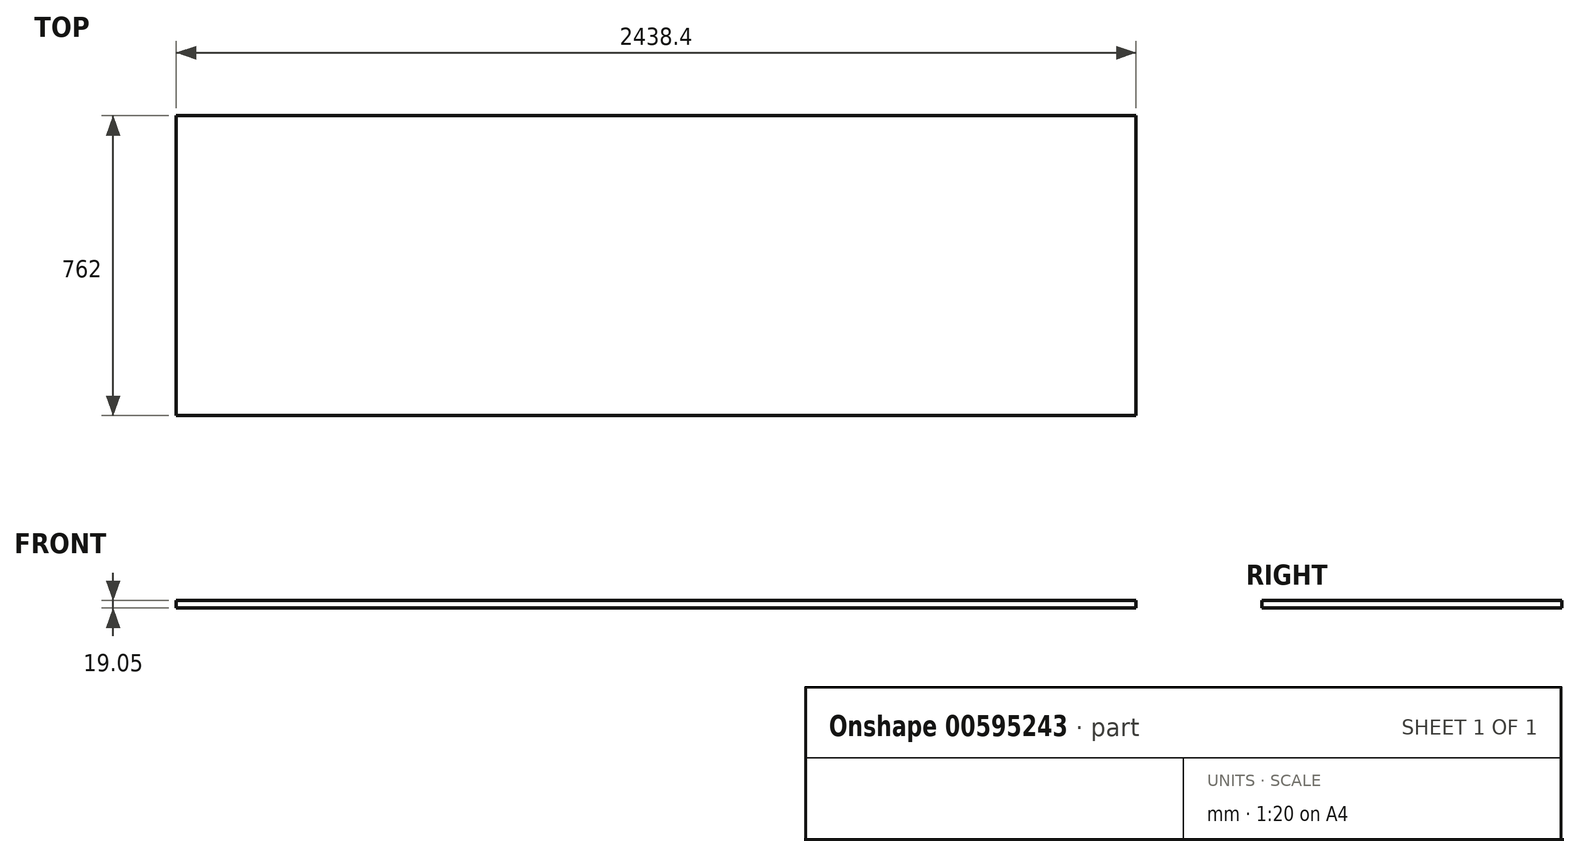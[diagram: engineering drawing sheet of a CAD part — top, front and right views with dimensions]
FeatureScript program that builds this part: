
annotation { "Feature Type Name" : "Feature", "Feature Type Description" : "" }
export const myFeature = defineFeature(function(context is Context, id is Id, definition is map)
    precondition{}
    {
        {
            var Q0;
            Q0=qCreatedBy(makeId("Top.planeOp"),FACE);
            var sketch = newSketch(context, id + "F0", { "sketchPlane" : qUnion([Q0])});
            skLineSegment(sketch, "E0.bottom", {"start": v(3810, -4419.6) * mm, "end": v(-3810, -4419.6) * mm});
            skLineSegment(sketch, "E0.top", {"start": v(3810, 4419.6) * mm, "end": v(-3810, 4419.6) * mm});
            skLineSegment(sketch, "E0.left", {"start": v(3810, -4419.6) * mm, "end": v(3810, 4419.6) * mm});
            skLineSegment(sketch, "E0.right", {"start": v(-3810, -4419.6) * mm, "end": v(-3810, 4419.6) * mm});
            skPoint(sketch, "E0.middle", {"position": v(0, 0) * mm});
            skLineSegment(sketch, "E1.top", {"start": v(3810, 1676.4) * mm, "end": v(1981.2, 1676.4) * mm});
            skLineSegment(sketch, "E1.right", {"start": v(1981.2, 4419.6) * mm, "end": v(1981.2, 1676.4) * mm});
            skLineSegment(sketch, "E2.bottom", {"start": v(-3810, -4419.6) * mm, "end": v(-3352.8, -4419.6) * mm});
            skLineSegment(sketch, "E2.top", {"start": v(-3810, -3962.4) * mm, "end": v(-3352.8, -3962.4) * mm});
            skLineSegment(sketch, "E2.left", {"start": v(-3810, -4419.6) * mm, "end": v(-3810, -3962.4) * mm});
            skLineSegment(sketch, "E2.right", {"start": v(-3352.8, -4419.6) * mm, "end": v(-3352.8, -3962.4) * mm});
            skLineSegment(sketch, "E3.bottom", {"start": v(457.2, -4419.6) * mm, "end": v(0, -4419.6) * mm});
            skLineSegment(sketch, "E3.top", {"start": v(457.2, -3962.4) * mm, "end": v(0, -3962.4) * mm});
            skLineSegment(sketch, "E3.left", {"start": v(457.2, -4419.6) * mm, "end": v(457.2, -3962.4) * mm});
            skLineSegment(sketch, "E3.right", {"start": v(0, -4419.6) * mm, "end": v(0, -3962.4) * mm});
            skLineSegment(sketch, "E4.bottom", {"start": v(3810, -4419.6) * mm, "end": v(3352.8, -4419.6) * mm});
            skLineSegment(sketch, "E4.top", {"start": v(3810, -3962.4) * mm, "end": v(3352.8, -3962.4) * mm});
            skLineSegment(sketch, "E4.left", {"start": v(3810, -4419.6) * mm, "end": v(3810, -3962.4) * mm});
            skLineSegment(sketch, "E4.right", {"start": v(3352.8, -4419.6) * mm, "end": v(3352.8, -3962.4) * mm});
            skLineSegment(sketch, "E5.bottom", {"start": v(-3259.23, 4114.8) * mm, "end": v(-820.83, 4114.8) * mm});
            skLineSegment(sketch, "E5.top", {"start": v(-3259.23, 3352.8) * mm, "end": v(-820.83, 3352.8) * mm});
            skLineSegment(sketch, "E5.left", {"start": v(-3259.23, 4114.8) * mm, "end": v(-3259.23, 3352.8) * mm});
            skLineSegment(sketch, "E5.right", {"start": v(-820.83, 4114.8) * mm, "end": v(-820.83, 3352.8) * mm});
            skLineSegment(sketch, "E6.bottom", {"start": v(-1676.4, 716.47) * mm, "end": v(-457.2, 716.47) * mm});
            skLineSegment(sketch, "E6.top", {"start": v(-1676.4, -1721.93) * mm, "end": v(-457.2, -1721.93) * mm});
            skLineSegment(sketch, "E6.left", {"start": v(-1676.4, 716.47) * mm, "end": v(-1676.4, -1721.93) * mm});
            skLineSegment(sketch, "E6.right", {"start": v(-457.2, 716.47) * mm, "end": v(-457.2, -1721.93) * mm});
            skLineSegment(sketch, "E7.bottom", {"start": v(-304.8, 4419.6) * mm, "end": v(152.4, 4419.6) * mm});
            skLineSegment(sketch, "E7.top", {"start": v(-304.8, 3962.4) * mm, "end": v(152.4, 3962.4) * mm});
            skLineSegment(sketch, "E7.left", {"start": v(-304.8, 4419.6) * mm, "end": v(-304.8, 3962.4) * mm});
            skLineSegment(sketch, "E7.right", {"start": v(152.4, 4419.6) * mm, "end": v(152.4, 3962.4) * mm});
            skLineSegment(sketch, "E8.bottom", {"start": v(1219.2, 4419.6) * mm, "end": v(1981.2, 4419.6) * mm});
            skLineSegment(sketch, "E8.top", {"start": v(1219.2, 1981.2) * mm, "end": v(1981.2, 1981.2) * mm});
            skLineSegment(sketch, "E8.left", {"start": v(1219.2, 4419.6) * mm, "end": v(1219.2, 1981.2) * mm});
            skLineSegment(sketch, "E8.right", {"start": v(1981.2, 4419.6) * mm, "end": v(1981.2, 1981.2) * mm});
            skLineSegment(sketch, "E9.bottom", {"start": v(1676.4, -70.73) * mm, "end": v(2590.8, -70.73) * mm});
            skLineSegment(sketch, "E9.top", {"start": v(1676.4, -2509.13) * mm, "end": v(2590.8, -2509.13) * mm});
            skLineSegment(sketch, "E9.left", {"start": v(1676.4, -70.73) * mm, "end": v(1676.4, -2509.13) * mm});
            skLineSegment(sketch, "E9.right", {"start": v(2590.8, -70.73) * mm, "end": v(2590.8, -2509.13) * mm});
            skLineSegment(sketch, "E10.bottom", {"start": v(-3550.94, 2237.3) * mm, "end": v(-3246.14, 2237.3) * mm});
            skLineSegment(sketch, "E10.top", {"start": v(-3550.94, 865.7) * mm, "end": v(-3246.14, 865.7) * mm});
            skLineSegment(sketch, "E10.left", {"start": v(-3550.94, 2237.3) * mm, "end": v(-3550.94, 865.7) * mm});
            skLineSegment(sketch, "E10.right", {"start": v(-3246.14, 2237.3) * mm, "end": v(-3246.14, 865.7) * mm});
            skLineSegment(sketch, "E11.bottom", {"start": v(-3539.06, 304.8) * mm, "end": v(-3093.74, 304.8) * mm});
            skLineSegment(sketch, "E11.top", {"start": v(-3539.06, 0) * mm, "end": v(-3093.74, 0) * mm});
            skLineSegment(sketch, "E11.left", {"start": v(-3539.06, 304.8) * mm, "end": v(-3539.06, 0) * mm});
            skLineSegment(sketch, "E11.right", {"start": v(-3093.74, 304.8) * mm, "end": v(-3093.74, 0) * mm});
            skLineSegment(sketch, "E12.bottom", {"start": v(-3550.94, -206.57) * mm, "end": v(-3093.74, -206.57) * mm});
            skLineSegment(sketch, "E12.top", {"start": v(-3550.94, -1273.37) * mm, "end": v(-3093.74, -1273.37) * mm});
            skLineSegment(sketch, "E12.left", {"start": v(-3550.94, -206.57) * mm, "end": v(-3550.94, -1273.37) * mm});
            skLineSegment(sketch, "E12.right", {"start": v(-3093.74, -206.57) * mm, "end": v(-3093.74, -1273.37) * mm});
            skLineSegment(sketch, "E13.bottom", {"start": v(-3550.94, -1901.3) * mm, "end": v(-3093.74, -1901.3) * mm});
            skLineSegment(sketch, "E13.top", {"start": v(-3550.94, -2510.9) * mm, "end": v(-3093.74, -2510.9) * mm});
            skLineSegment(sketch, "E13.left", {"start": v(-3550.94, -1901.3) * mm, "end": v(-3550.94, -2510.9) * mm});
            skLineSegment(sketch, "E13.right", {"start": v(-3093.74, -1901.3) * mm, "end": v(-3093.74, -2510.9) * mm});
            skLineSegment(sketch, "E14.bottom", {"start": v(-1066.8, 716.47) * mm, "end": v(-457.2, 716.47) * mm});
            skLineSegment(sketch, "E14.top", {"start": v(-1066.8, 1282.85) * mm, "end": v(-457.2, 1282.85) * mm});
            skLineSegment(sketch, "E14.left", {"start": v(-1066.8, 716.47) * mm, "end": v(-1066.8, 1282.85) * mm});
            skLineSegment(sketch, "E14.right", {"start": v(-457.2, 716.47) * mm, "end": v(-457.2, 1282.85) * mm});
            skLineSegment(sketch, "E15.bottom", {"start": v(-1066.8, -1721.93) * mm, "end": v(-1672.61, -1721.93) * mm});
            skLineSegment(sketch, "E15.top", {"start": v(-1066.8, -2287.75) * mm, "end": v(-1672.61, -2287.75) * mm});
            skLineSegment(sketch, "E15.left", {"start": v(-1066.8, -1721.93) * mm, "end": v(-1066.8, -2287.75) * mm});
            skLineSegment(sketch, "E15.right", {"start": v(-1672.61, -1721.93) * mm, "end": v(-1672.61, -2287.75) * mm});
            skLineSegment(sketch, "E16.bottom", {"start": v(3810, 457.2) * mm, "end": v(2286, 457.2) * mm});
            skLineSegment(sketch, "E16.top", {"start": v(3810, 1676.4) * mm, "end": v(2286, 1676.4) * mm});
            skLineSegment(sketch, "E16.left", {"start": v(3810, 457.2) * mm, "end": v(3810, 1676.4) * mm});
            skLineSegment(sketch, "E16.right", {"start": v(2286, 457.2) * mm, "end": v(2286, 1676.4) * mm});
            skLineSegment(sketch, "E17", {"start": v(762, -3423.53) * mm, "end": v(3810, -3423.53) * mm});
            skSolve(sketch);
        }
        {
            var Q0;
            Q0=makeQuery(id+"F0.imprint","IMPRINT",FACE,{"disambiguationData":[TD([[makeQuery(id+"F0.imprint","IMPRINT",EDGE,{"derivedFrom":sQuery(id+"F0.wireOp",EDGE,"E5.bottom")}),-1.0]])]});
            var sketch = newSketch(context, id + "F1", { "sketchPlane" : qUnion([Q0])});
            skLineSegment(sketch, "E18.bottom", {"start": v(-3208.43, 4114.8) * mm, "end": v(-3259.23, 4114.8) * mm});
            skLineSegment(sketch, "E18.top", {"start": v(-3208.43, 4013.2) * mm, "end": v(-3259.23, 4013.2) * mm});
            skLineSegment(sketch, "E18.left", {"start": v(-3208.43, 4114.8) * mm, "end": v(-3208.43, 4013.2) * mm});
            skLineSegment(sketch, "E18.right", {"start": v(-3259.23, 4114.8) * mm, "end": v(-3259.23, 4013.2) * mm});
            skPoint(sketch, "E19.firstSnap0", {"position": v(-3259.23, 4064) * mm});
            skLineSegment(sketch, "E19.bottom", {"start": v(-3259.23, 3352.81) * mm, "end": v(-3208.43, 3352.81) * mm});
            skLineSegment(sketch, "E19.top", {"start": v(-3259.23, 3454.41) * mm, "end": v(-3208.43, 3454.41) * mm});
            skLineSegment(sketch, "E19.left", {"start": v(-3259.23, 3352.81) * mm, "end": v(-3259.23, 3454.41) * mm});
            skLineSegment(sketch, "E19.right", {"start": v(-3208.43, 3352.81) * mm, "end": v(-3208.43, 3454.41) * mm});
            skLineSegment(sketch, "E20.bottom", {"start": v(-820.93, 4115.27) * mm, "end": v(-871.73, 4115.27) * mm});
            skLineSegment(sketch, "E20.top", {"start": v(-820.93, 4012.73) * mm, "end": v(-871.73, 4012.73) * mm});
            skLineSegment(sketch, "E20.left", {"start": v(-820.93, 4115.27) * mm, "end": v(-820.93, 4012.73) * mm});
            skLineSegment(sketch, "E20.right", {"start": v(-871.73, 4115.27) * mm, "end": v(-871.73, 4012.73) * mm});
            skLineSegment(sketch, "E21.bottom", {"start": v(-820.93, 3353.17) * mm, "end": v(-871.73, 3353.17) * mm});
            skLineSegment(sketch, "E21.top", {"start": v(-820.93, 3461.25) * mm, "end": v(-871.73, 3461.25) * mm});
            skLineSegment(sketch, "E21.left", {"start": v(-820.93, 3353.17) * mm, "end": v(-820.93, 3461.25) * mm});
            skLineSegment(sketch, "E21.right", {"start": v(-871.73, 3353.17) * mm, "end": v(-871.73, 3461.25) * mm});
            skLineSegment(sketch, "E22.bottom", {"start": v(-3208.43, 4114.8) * mm, "end": v(-871.73, 4114.8) * mm});
            skLineSegment(sketch, "E22.top", {"start": v(-3208.43, 4064) * mm, "end": v(-871.73, 4064) * mm});
            skLineSegment(sketch, "E22.left", {"start": v(-3208.43, 4114.8) * mm, "end": v(-3208.43, 4064) * mm});
            skLineSegment(sketch, "E22.right", {"start": v(-871.73, 4114.8) * mm, "end": v(-871.73, 4064) * mm});
            skLineSegment(sketch, "E23.bottom", {"start": v(-3259.23, 4013.2) * mm, "end": v(-3208.43, 4013.2) * mm});
            skLineSegment(sketch, "E23.left", {"start": v(-3259.23, 4013.2) * mm, "end": v(-3259.23, 3454.41) * mm});
            skLineSegment(sketch, "E23.right", {"start": v(-3208.43, 4013.2) * mm, "end": v(-3208.43, 3454.41) * mm});
            skLineSegment(sketch, "E24.bottom", {"start": v(-3208.43, 3352.81) * mm, "end": v(-871.73, 3352.81) * mm});
            skLineSegment(sketch, "E24.top", {"start": v(-3208.43, 3407.2) * mm, "end": v(-871.73, 3407.2) * mm});
            skLineSegment(sketch, "E24.left", {"start": v(-3208.43, 3352.81) * mm, "end": v(-3208.43, 3407.2) * mm});
            skLineSegment(sketch, "E24.right", {"start": v(-871.73, 3352.81) * mm, "end": v(-871.73, 3407.2) * mm});
            skLineSegment(sketch, "E25.left", {"start": v(-820.93, 4012.73) * mm, "end": v(-820.93, 3461.25) * mm});
            skLineSegment(sketch, "E25.right", {"start": v(-871.73, 4012.73) * mm, "end": v(-871.73, 3461.25) * mm});
            skSolve(sketch);
        }
        {
            var Q0;
            Q0=sQuery(id+"F1.wireOp",EDGE,"E19.right");
            var Q1;
            Q1=sQuery(id+"F1.wireOp",EDGE,"E19.top");
            var Q2;
            Q2=sQuery(id+"F1.wireOp",EDGE,"E19.left");
            var Q3;
            Q3=sQuery(id+"F1.wireOp",EDGE,"E19.bottom");
            extrude(context, id + "F2", {"bodyType" : ToolBodyType.SURFACE, "surfaceEntities" : qUnion([Q0, Q1, Q2, Q3]), "depth" : 914.4 * mm, "offsetDistance" : 25.4 * mm});
        }
        {
            var Q0;
            Q0=sQuery(id+"F1.wireOp",EDGE,"E18.left");
            var Q1;
            Q1=sQuery(id+"F1.wireOp",EDGE,"E18.top");
            var Q2;
            Q2=sQuery(id+"F1.wireOp",EDGE,"E18.right");
            var Q3;
            Q3=sQuery(id+"F1.wireOp",EDGE,"E18.bottom");
            var Q4;
            Q4=sQuery(id+"F1.wireOp",EDGE,"E20.right");
            var Q5;
            Q5=sQuery(id+"F1.wireOp",EDGE,"E20.top");
            var Q6;
            Q6=sQuery(id+"F1.wireOp",EDGE,"E20.bottom");
            var Q7;
            Q7=sQuery(id+"F1.wireOp",EDGE,"E20.left");
            var Q8;
            Q8=sQuery(id+"F1.wireOp",EDGE,"E21.top");
            var Q9;
            Q9=sQuery(id+"F1.wireOp",EDGE,"E21.right");
            var Q10;
            Q10=sQuery(id+"F1.wireOp",EDGE,"E21.left");
            var Q11;
            Q11=sQuery(id+"F1.wireOp",EDGE,"E21.bottom");
            extrude(context, id + "F3", {"bodyType" : ToolBodyType.SURFACE, "surfaceEntities" : qUnion([Q0, Q1, Q2, Q3, Q4, Q5, Q6, Q7, Q8, Q9, Q10, Q11]), "depth" : 914.4 * mm, "offsetDistance" : 25.4 * mm});
        }
        {
            var Q0;
            Q0=sQuery(id+"F1.wireOp",EDGE,"E23.right");
            var Q1;
            Q1=sQuery(id+"F1.wireOp",EDGE,"E23.left");
            var Q2;
            Q2=sQuery(id+"F1.wireOp",EDGE,"E22.top");
            var Q3;
            Q3=sQuery(id+"F1.wireOp",EDGE,"E24.top");
            var Q4;
            Q4=sQuery(id+"F1.wireOp",EDGE,"E25.right");
            var Q5;
            Q5=sQuery(id+"F1.wireOp",EDGE,"E25.left");
            extrude(context, id + "F4", {"bodyType" : ToolBodyType.SURFACE, "surfaceEntities" : qUnion([Q0, Q1, Q2, Q3, Q4, Q5]), "depth" : 101.6 * mm, "offsetDistance" : 25.4 * mm});
        }
        {
            var Q0;
            Q0=makeQuery(id+"F0.imprint","IMPRINT",FACE,{"disambiguationData":[TD([[makeQuery(id+"F0.imprint","IMPRINT",EDGE,{"derivedFrom":sQuery(id+"F0.wireOp",EDGE,"E5.bottom")}),-1.0]])]});
            extrude(context, id + "F5", {"entities" : qUnion([Q0]), "depth" : 19.05 * mm, "offsetDistance" : 25.4 * mm});
        }
        {
            var Q0;
            Q0=sQuery(id+"F1.wireOp",EDGE,"E22.bottom");
            var Q1;
            Q1=sQuery(id+"F1.wireOp",EDGE,"E24.bottom");
            extrude(context, id + "F6", {"bodyType" : ToolBodyType.SURFACE, "surfaceEntities" : qUnion([Q0, Q1]), "depth" : 101.6 * mm, "offsetDistance" : 25.4 * mm});
        }
    });
